# Revit family: Controls_BlueGiant_Traffic-Light-Control-Box
name_source: partatom
category: Specialty Equipment
units: mm (PartAtom-declared; Revit-internal decimal feet)

## family parameters
Always vertical = No
Cut with Voids When Loaded = No
Enable Cutting in Views = No
Maintain Annotation Orientation = No
Part Type = Normal
Room Calculation Point = No
Round Connector Dimension = Use Diameter
Shared = No
Work Plane-Based = Yes

## types (1)
- ByType
    Assembly Code = E1030300
    Construction Details = http://www.arcat.com
    Default Elevation = 4' - 0"
    Description = Blue Giant LED Traffic Light Control Box
    Expected Lifespan (Years) = 0
    Green Building-LEED = http://www.arcat.com
    Installation_Fabricaton = http://www.bluegiant.com
    Keynote = 11160
    MEP Amperage = 0 A
    Maintenance Schedule (Months) = 0
    Manufacturer = Blue Giant Equipment Corp.
    Manufacturer Fax = 905-457-2313
    Manufacturer Website = http://www.bluegiant.com
    Model = CHECK WITH MANUFACTURER
    Mounting Height = 7' - 0"
    Panel Material = Metal - Blue Giant - Zinc Coated Steel
    Product Data = http://www.arcat.com
    Product Properties = http://www.arcat.com
    Sales Information = http://www.bluegiant.com
    Send Message = http://admin.arcat.com
    SpecWizard = http://www.arcat.com
    Specification = http://www.arcat.com
    URL = http://www.bluegiant.com
    Unit Depth = 0' - 4 9/16"
    Unit Height = 0' - 5 29/32"
    Unit Width = 0' - 5 29/32"
    Voltage_MEP = 0 V
    Warranty Duration (Years) = 0

## geometry (parser evidence)
native form markers: Sweep x2
no freeform markers — native parametric forms only
